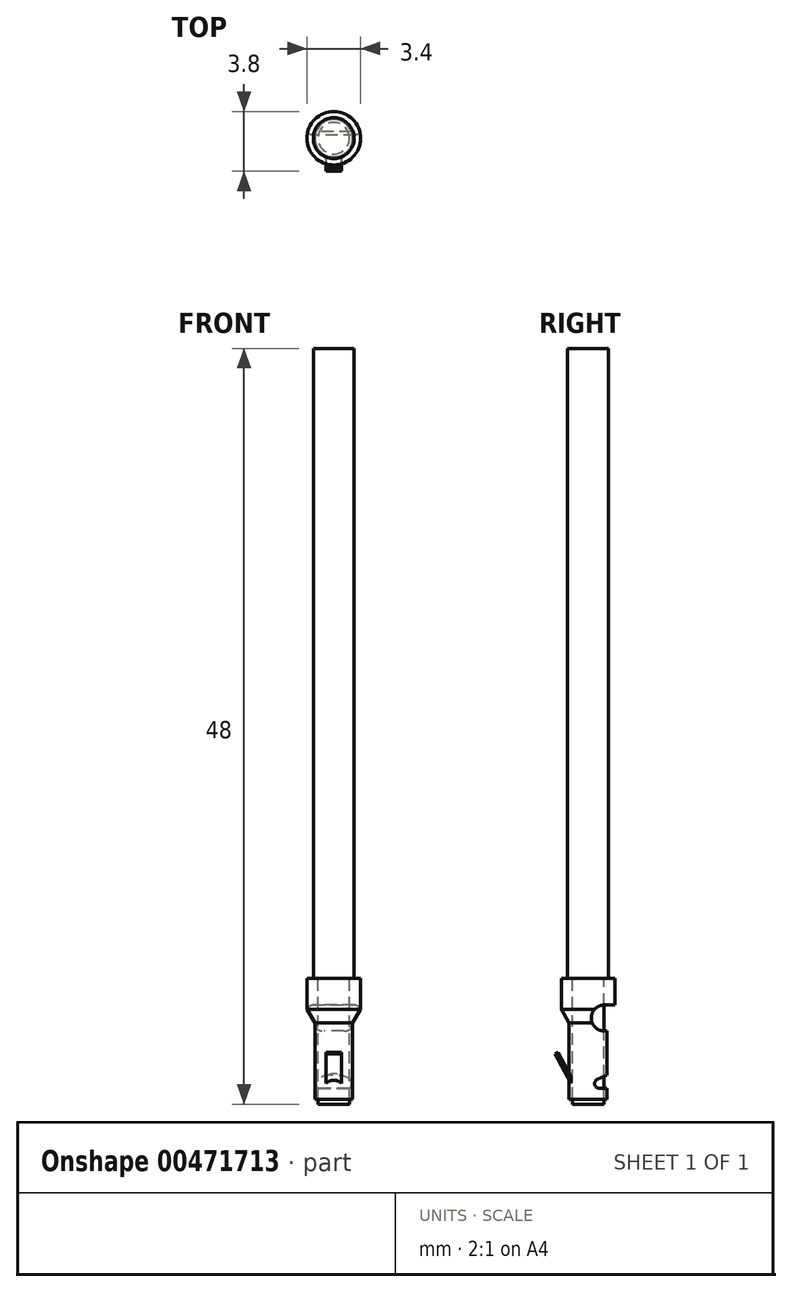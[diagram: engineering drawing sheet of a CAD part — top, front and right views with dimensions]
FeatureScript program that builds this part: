
annotation { "Feature Type Name" : "Feature", "Feature Type Description" : "" }
export const myFeature = defineFeature(function(context is Context, id is Id, definition is map)
    precondition{}
    {
        {
            var Q0;
            Q0=qCreatedBy(makeId("Right.planeOp"),FACE);
            var sketch = newSketch(context, id + "F0", { "sketchPlane" : qUnion([Q0])});
            skLineSegment(sketch, "E0", {"start": v(0, -3) * mm, "end": v(0, 4.7) * mm});
            skLineSegment(sketch, "E1", {"start": v(0, 4.7) * mm, "end": v(1.7, 4.7) * mm});
            skLineSegment(sketch, "E2", {"start": v(1.7, 4.7) * mm, "end": v(1.7, 2.72) * mm});
            skLineSegment(sketch, "E3", {"start": v(1.7, 2.72) * mm, "end": v(1.2, 1.85) * mm});
            skLineSegment(sketch, "E4", {"start": v(0, -3) * mm, "end": v(1.2, -3) * mm});
            skLineSegment(sketch, "E5", {"start": v(1.2, -3) * mm, "end": v(1.2, 1.85) * mm});
            skSolve(sketch);
        }
        {
            var Q0;
            Q0=makeQuery(id+"F0.imprint","IMPRINT",FACE,{"disambiguationData":[TD([[makeQuery(id+"F0.imprint","IMPRINT",EDGE,{"derivedFrom":sQuery(id+"F0.wireOp",EDGE,"E0")}),-1.0]])]});
            var Q1;
            Q1=sQuery(id+"F0.wireOp",EDGE,"E0");
            revolve(context, id + "F1", {"entities" : qUnion([Q0]), "axis" : qUnion([Q1]), "revolveType" : RevolveType.FULL});
        }
        {
            var Q0;
            Q0=qCreatedBy(makeId("Right.planeOp"),FACE);
            var sketch = newSketch(context, id + "F2", { "sketchPlane" : qUnion([Q0])});
            skLineSegment(sketch, "E6", {"start": v(2.19, 3) * mm, "end": v(1.03, 3) * mm});
            skLineSegment(sketch, "E7", {"start": v(1.03, 1.34) * mm, "end": v(2.19, 1.34) * mm});
            skLineSegment(sketch, "E8", {"start": v(2.19, 1.34) * mm, "end": v(2.19, 3) * mm});
            skArc(sketch, "E9", {"start": v(1.03, 3) * mm, "mid": v(0.2, 2.17) * mm, "end": v(1.03, 1.34) * mm});
            skLineSegment(sketch, "E10", {"start": v(1.82, -2.3) * mm, "end": v(0.71, -2.3) * mm});
            skLineSegment(sketch, "E11", {"start": v(0.6, -1.73) * mm, "end": v(1.82, -1.18) * mm});
            skLineSegment(sketch, "E12", {"start": v(1.82, -1.18) * mm, "end": v(1.82, -2.3) * mm});
            skArc(sketch, "E13.filletArc", {"start": v(0.6, -1.73) * mm, "mid": v(0.42, -2.06) * mm, "end": v(0.71, -2.3) * mm});
            skSolve(sketch);
        }
        {
            var Q0;
            Q0=makeQuery(id+"F2.imprint","IMPRINT",FACE,{"disambiguationData":[TD([[makeQuery(id+"F2.imprint","IMPRINT",EDGE,{"derivedFrom":sQuery(id+"F2.wireOp",EDGE,"E6")}),1.0]])]});
            var Q1;
            Q1=makeQuery(id+"F2.imprint","IMPRINT",FACE,{"disambiguationData":[TD([[makeQuery(id+"F2.imprint","IMPRINT",EDGE,{"derivedFrom":sQuery(id+"F2.wireOp",EDGE,"E10")}),-1.0]])]});
            extrude(context, id + "F3", {"entities" : qUnion([Q0, Q1]), "operationType" : NewBodyOperationType.REMOVE, "endBound" : BoundingType.THROUGH_ALL, "depth" : 25 * mm, "hasSecondDirection" : true, "secondDirectionBound" : SecondDirectionBoundingType.THROUGH_ALL, "secondDirectionOppositeDirection" : true, "secondDirectionDepth" : 25 * mm});
        }
        {
            var Q0;
            Q0=qCreatedBy(makeId("Right.planeOp"),FACE);
            var sketch = newSketch(context, id + "F4", { "sketchPlane" : qUnion([Q0])});
            skLineSegment(sketch, "E14", {"start": v(-0.76, -2.6) * mm, "end": v(-2.1, -0.1) * mm});
            skLineSegment(sketch, "E15", {"start": v(-2.1, -0.1) * mm, "end": v(-1.91, 0) * mm});
            skLineSegment(sketch, "E16", {"start": v(-1.91, 0) * mm, "end": v(-0.76, -2.16) * mm});
            skLineSegment(sketch, "E17", {"start": v(-0.76, -2.16) * mm, "end": v(-0.76, -2.6) * mm});
            skSolve(sketch);
        }
        {
            var Q0;
            Q0=makeQuery(id+"F4.imprint","IMPRINT",FACE,{"disambiguationData":[TD([[makeQuery(id+"F4.imprint","IMPRINT",EDGE,{"derivedFrom":sQuery(id+"F4.wireOp",EDGE,"E14")}),-1.0]])]});
            extrude(context, id + "F5", {"entities" : qUnion([Q0]), "operationType" : NewBodyOperationType.ADD, "endBound" : BoundingType.SYMMETRIC, "depth" : 1 * mm});
        }
        {
            var Q0;
            Q0=makeQuery(id+"F1.opRevolve","SWEPT_FACE",FACE,{"disambiguationData":[OSD([sQuery(id+"F0.wireOp",EDGE,"E1")])]});
            var sketch = newSketch(context, id + "F6", { "sketchPlane" : qUnion([Q0])});
            skCircle(sketch, "E18", {"center": v(0, 0) * mm, "radius": 1 * mm});
            skCircle(sketch, "E19", {"center": v(0, 0) * mm, "radius": 1.3 * mm});
            skSolve(sketch);
        }
        {
            var Q0;
            Q0=makeQuery(id+"F6.imprint","IMPRINT",FACE,{"disambiguationData":[TD([[makeQuery(id+"F6.imprint","IMPRINT",EDGE,{"derivedFrom":sQuery(id+"F6.wireOp",EDGE,"E18")}),1.0]])]});
            extrude(context, id + "F7", {"entities" : qUnion([Q0]), "oppositeDirection" : true, "depth" : 8 * mm});
        }
        {
            var Q0;
            Q0=makeQuery(id+"F6.imprint","IMPRINT",FACE,{"disambiguationData":[TD([[makeQuery(id+"F6.imprint","IMPRINT",EDGE,{"derivedFrom":sQuery(id+"F6.wireOp",EDGE,"E18")}),1.0]])]});
            var Q1;
            Q1=makeQuery(id+"F6.imprint","IMPRINT",FACE,{"disambiguationData":[TD([[makeQuery(id+"F6.imprint","IMPRINT",EDGE,{"derivedFrom":sQuery(id+"F6.wireOp",EDGE,"E18")}),-1.0]])]});
            extrude(context, id + "F8", {"entities" : qUnion([Q0, Q1]), "depth" : 40 * mm});
        }
    });
